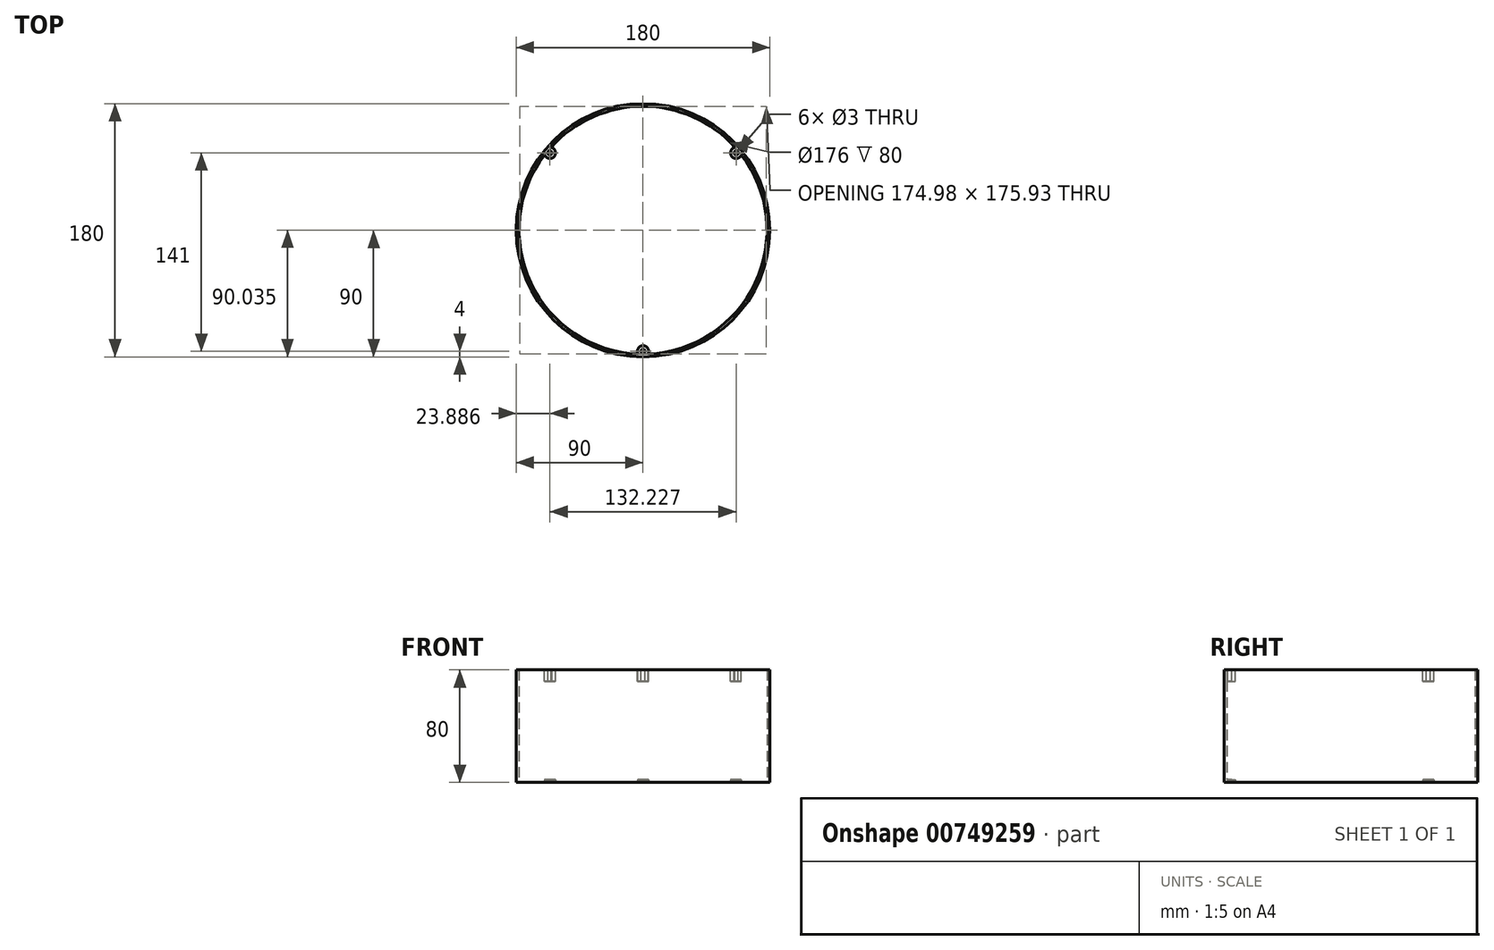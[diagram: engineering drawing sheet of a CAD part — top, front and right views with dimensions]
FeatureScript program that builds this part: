
annotation { "Feature Type Name" : "Feature", "Feature Type Description" : "" }
export const myFeature = defineFeature(function(context is Context, id is Id, definition is map)
    precondition{}
    {
        {
            var Q0;
            Q0=qCreatedBy(makeId("Top.planeOp"),FACE);
            var sketch = newSketch(context, id + "F0", { "sketchPlane" : qUnion([Q0])});
            skCircle(sketch, "E0", {"center": v(0, 0) * mm, "radius": 90 * mm});
            skSolve(sketch);
        }
        {
            var Q0;
            Q0 = qSketchRegion(id + "F0", true);
            extrude(context, id + "F1", {"entities" : qUnion([Q0]), "depth" : 80 * mm, "offsetDistance" : 25 * mm});
        }
        {
            var Q0;
            Q0=makeQuery(id+"F1.opExtrude","CAP_FACE",FACE,{"disambiguationData":[OSD([sQuery(id+"F0.wireOp",EDGE,"E0")])],"isStart":false});
            var Q1;
            Q1=makeQuery(id+"F1.opExtrude","CAP_FACE",FACE,{"disambiguationData":[OSD([sQuery(id+"F0.wireOp",EDGE,"E0")])],"isStart":true});
            shell(context, id + "F2", {"entities" : qUnion([Q0, Q1]), "thickness" : 2 * mm});
        }
        {
            var Q0;
            Q0=qCreatedBy(makeId("Top.planeOp"),FACE);
            var sketch = newSketch(context, id + "F3", { "sketchPlane" : qUnion([Q0])});
            skCircle(sketch, "E1", {"center": v(66.11, 55) * mm, "radius": 4 * mm});
            skCircle(sketch, "E2", {"center": v(0, -86) * mm, "radius": 4 * mm});
            skCircle(sketch, "E3", {"center": v(-66.11, 55) * mm, "radius": 4 * mm});
            skSolve(sketch);
        }
        {
            var Q0;
            Q0 = qSketchRegion(id + "F3", true);
            extrude(context, id + "F4", {"entities" : qUnion([Q0]), "operationType" : NewBodyOperationType.ADD, "depth" : 2 * mm, "offsetDistance" : 25 * mm});
        }
        {
            var Q0;
            Q0=makeQuery(id+"F1.opExtrude","CAP_FACE",FACE,{"disambiguationData":[OSD([sQuery(id+"F0.wireOp",EDGE,"E0")])],"isStart":false});
            var sketch = newSketch(context, id + "F5", { "sketchPlane" : qUnion([Q0])});
            skCircle(sketch, "E4", {"center": v(66.11, 55) * mm, "radius": 4 * mm});
            skCircle(sketch, "E5", {"center": v(0, -86) * mm, "radius": 4 * mm});
            skCircle(sketch, "E6", {"center": v(-66.11, 55) * mm, "radius": 4 * mm});
            skSolve(sketch);
        }
        {
            var Q0;
            Q0 = qSketchRegion(id + "F5", true);
            extrude(context, id + "F6", {"entities" : qUnion([Q0]), "operationType" : NewBodyOperationType.ADD, "oppositeDirection" : true, "depth" : 8 * mm, "offsetDistance" : 25 * mm});
        }
        {
            var Q0;
            Q0=makeQuery(id+"F6.boolean.opBoolean","MERGE",FACE,{"derivedFrom":[makeQuery(id+"F1.opExtrude","CAP_FACE",FACE,{"disambiguationData":[OSD([sQuery(id+"F0.wireOp",EDGE,"E0")])],"isStart":false}),makeQuery(id+"F6.opExtrude","CAP_FACE",FACE,{"disambiguationData":[OSD([sQuery(id+"F5.wireOp",EDGE,"E4")])],"isStart":true}),makeQuery(id+"F6.opExtrude","CAP_FACE",FACE,{"disambiguationData":[OSD([sQuery(id+"F5.wireOp",EDGE,"E5")])],"isStart":true}),makeQuery(id+"F6.opExtrude","CAP_FACE",FACE,{"disambiguationData":[OSD([sQuery(id+"F5.wireOp",EDGE,"E6")])],"isStart":true})]});
            var sketch = newSketch(context, id + "F7", { "sketchPlane" : qUnion([Q0])});
            skCircle(sketch, "E7", {"center": v(-66.11, 55) * mm, "radius": 1.5 * mm});
            skCircle(sketch, "E8", {"center": v(66.11, 55) * mm, "radius": 1.5 * mm});
            skCircle(sketch, "E9", {"center": v(0, -86) * mm, "radius": 1.5 * mm});
            skSolve(sketch);
        }
        {
            var Q0;
            Q0 = qSketchRegion(id + "F7", true);
            extrude(context, id + "F8", {"entities" : qUnion([Q0]), "operationType" : NewBodyOperationType.REMOVE, "oppositeDirection" : true, "depth" : 80 * mm, "offsetDistance" : 25 * mm, "hasSecondDirection" : true, "secondDirectionOppositeDirection" : false, "secondDirectionDepth" : 25 * mm});
        }
    });
